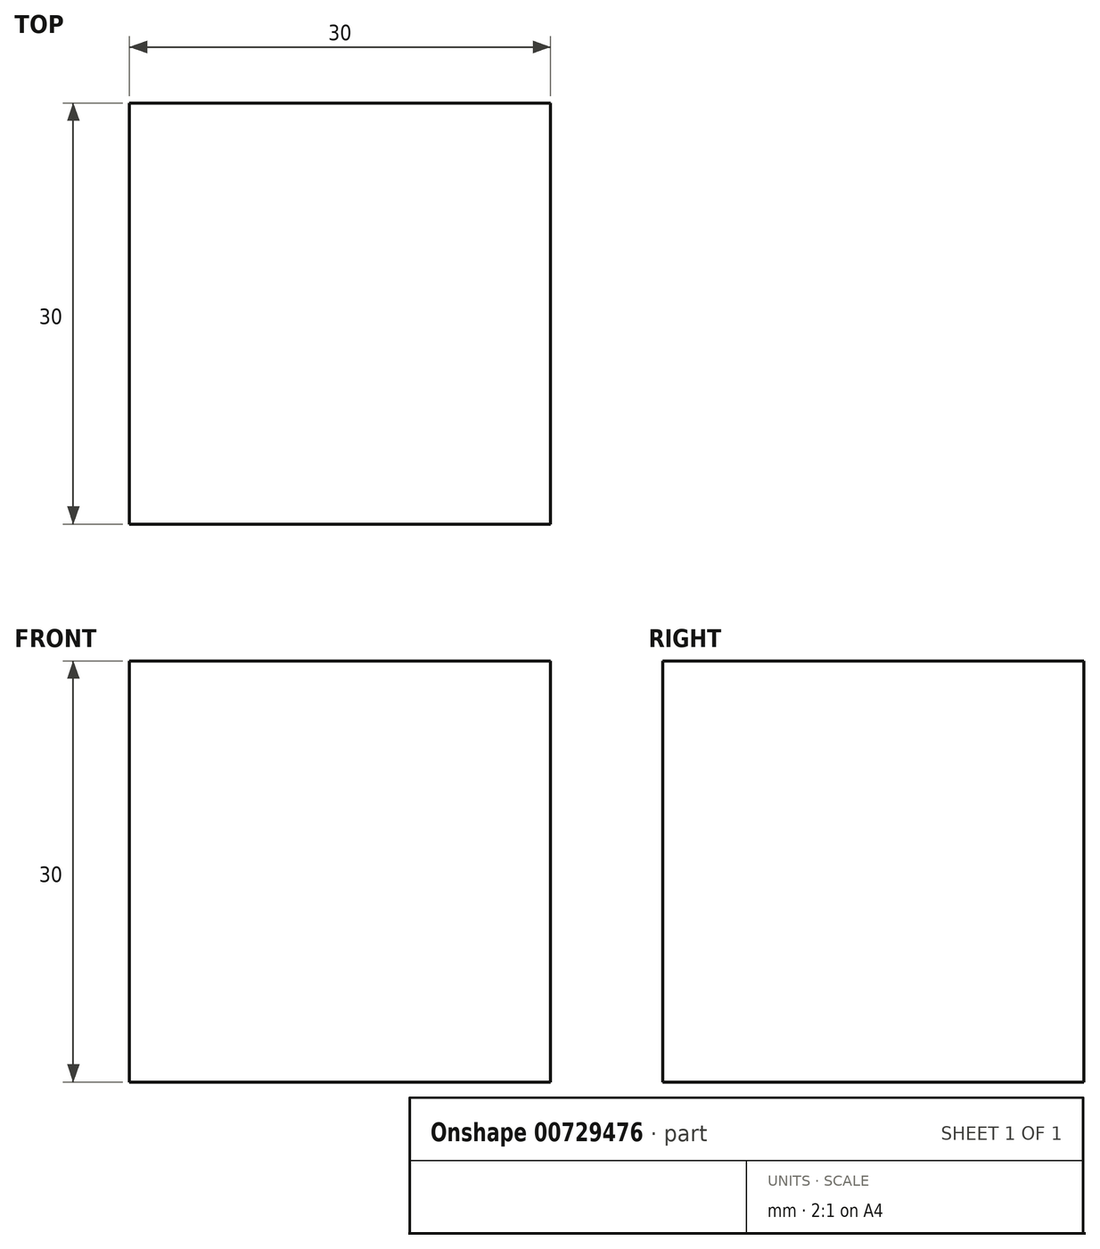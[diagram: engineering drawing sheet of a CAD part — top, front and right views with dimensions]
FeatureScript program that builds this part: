
annotation { "Feature Type Name" : "Feature", "Feature Type Description" : "" }
export const myFeature = defineFeature(function(context is Context, id is Id, definition is map)
    precondition{}
    {
        {
            var Q0;
            Q0=qCreatedBy(makeId("Top.planeOp"),FACE);
            var sketch = newSketch(context, id + "F0", { "sketchPlane" : qUnion([Q0])});
            skLineSegment(sketch, "E0.bottom", {"start": v(15, -15) * mm, "end": v(-15, -15) * mm});
            skLineSegment(sketch, "E0.top", {"start": v(15, 15) * mm, "end": v(-15, 15) * mm});
            skLineSegment(sketch, "E0.left", {"start": v(15, -15) * mm, "end": v(15, 15) * mm});
            skLineSegment(sketch, "E0.right", {"start": v(-15, -15) * mm, "end": v(-15, 15) * mm});
            skPoint(sketch, "E0.middle", {"position": v(0, 0) * mm});
            skSolve(sketch);
        }
        {
            var Q0;
            Q0=makeQuery(id+"F0.imprint","IMPRINT",FACE,{"disambiguationData":[TD([[makeQuery(id+"F0.imprint","IMPRINT",EDGE,{"derivedFrom":sQuery(id+"F0.wireOp",EDGE,"E0.bottom")}),-1.0]])]});
            extrude(context, id + "F1", {"entities" : qUnion([Q0]), "depth" : 30 * mm, "offsetDistance" : 25 * mm});
        }
    });
